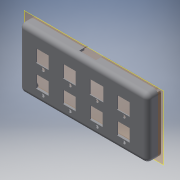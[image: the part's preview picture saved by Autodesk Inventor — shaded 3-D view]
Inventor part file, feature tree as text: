
AUTODESK INVENTOR PART (.ipt)
format: ipt  version: 2019 (Build 230136000, 136)  size: 272,896 bytes
history: native  units: mm
features: reference x30, sketch x7, extrude x7, other x5, plane x4, fillet x1
ambient origin geometry x8: Origin, YZ Plane, XZ Plane, XY Plane, X Axis, Y Axis, Z Axis, Center Point
bodies: Volumenkörper1 (feature_tree)
feature tree (54):
  plane  "Arbeitsebene1"
  sketch  "Skizze1"  dims[d0=0.3mm d1=0.3mm]
  plane  "Arbeitsebene2"
  extrude  "Extrusion1"  Depth=0.3mm
  extrude  "Extrusion2"  Depth=0.3mm
  extrude  "Extrusion3"  Depth=10.0mm TaperAngle=0.0deg
  extrude  "Extrusion4"  Depth=1.0mm TaperAngle=0.0deg
  extrude  "Extrusion5"  Depth=5.5mm
  sketch  "Skizze6"  dims[d19=18.0mm d20=6.75mm d21=0.0mm]
  plane  "Arbeitsebene3"
  extrude  "Extrusion6"  Depth=18.0mm TaperAngle=0.0deg
  plane  "Arbeitsebene4"
  extrude  "Extrusion7"  Depth=0.8mm
  fillet  "Rundung1"  Radius=0.8mm
  reference  "Referenz1"
  reference  "Referenz2"
  reference  "Referenz3"
  reference  "Referenz4"
  reference  "Referenz5"
  reference  "Referenz6"
  reference  "Referenz7"
  reference  "Referenz8"
  reference  "Referenz9"
  reference  "Referenz10"
  reference  "Referenz11"
  reference  "Referenz12"
  reference  "Referenz13"
  reference  "Referenz14"
  reference  "Referenz15"
  reference  "Referenz16"
  reference  "Referenz17"
  sketch  "Skizze2"  dims[d2=0.3mm d4=0.3mm]
  sketch  "Skizze3"  dims[d5=0.3mm d10=10.0mm d11=0.0mm]
  reference  "Referenz18"
  sketch  "Skizze4"  dims[d12=1.0mm d13=0.0mm d14=1.0mm d15=0.0mm]
  reference  "Referenz19"
  reference  "Referenz20"
  reference  "Referenz21"
  reference  "Referenz22"
  reference  "Referenz23"
  reference  "Referenz24"
  reference  "Referenz25"
  reference  "Referenz26"
  sketch  "Skizze5"  dims[d16=1.0mm d17=0.0mm d18=5.5mm]
  sketch  "Skizze7"  dims[d22=0.8mm d23=0.8mm d24=0.8mm d25=0.8mm d26=0.8mm d27=0.8mm d28=6.75mm d29=0.0mm d30=7.0mm d31=3.9mm d32=3.9mm d33=7.0mm d34=3.9mm d35=7.0mm d36=7.0mm d37=3.9mm d38=5.0mm d39=0.0mm d40=5.0mm d44=2.35mm d45=2.985mm d46=2.35mm d47=3.95mm]
  reference  "Referenz27"
  reference  "Referenz28"
  reference  "Referenz29"
  reference  "Referenz30"
  other  "<userpath>\Google Drive\Projekte\makroboard\makroboard_case\Baugruppe1.iam"
  other  "Baugruppe1.iam"
  other  "case_bot:1"
  other  "makroboard:1"
  other  "asm_mx_asm_PCB:4"
